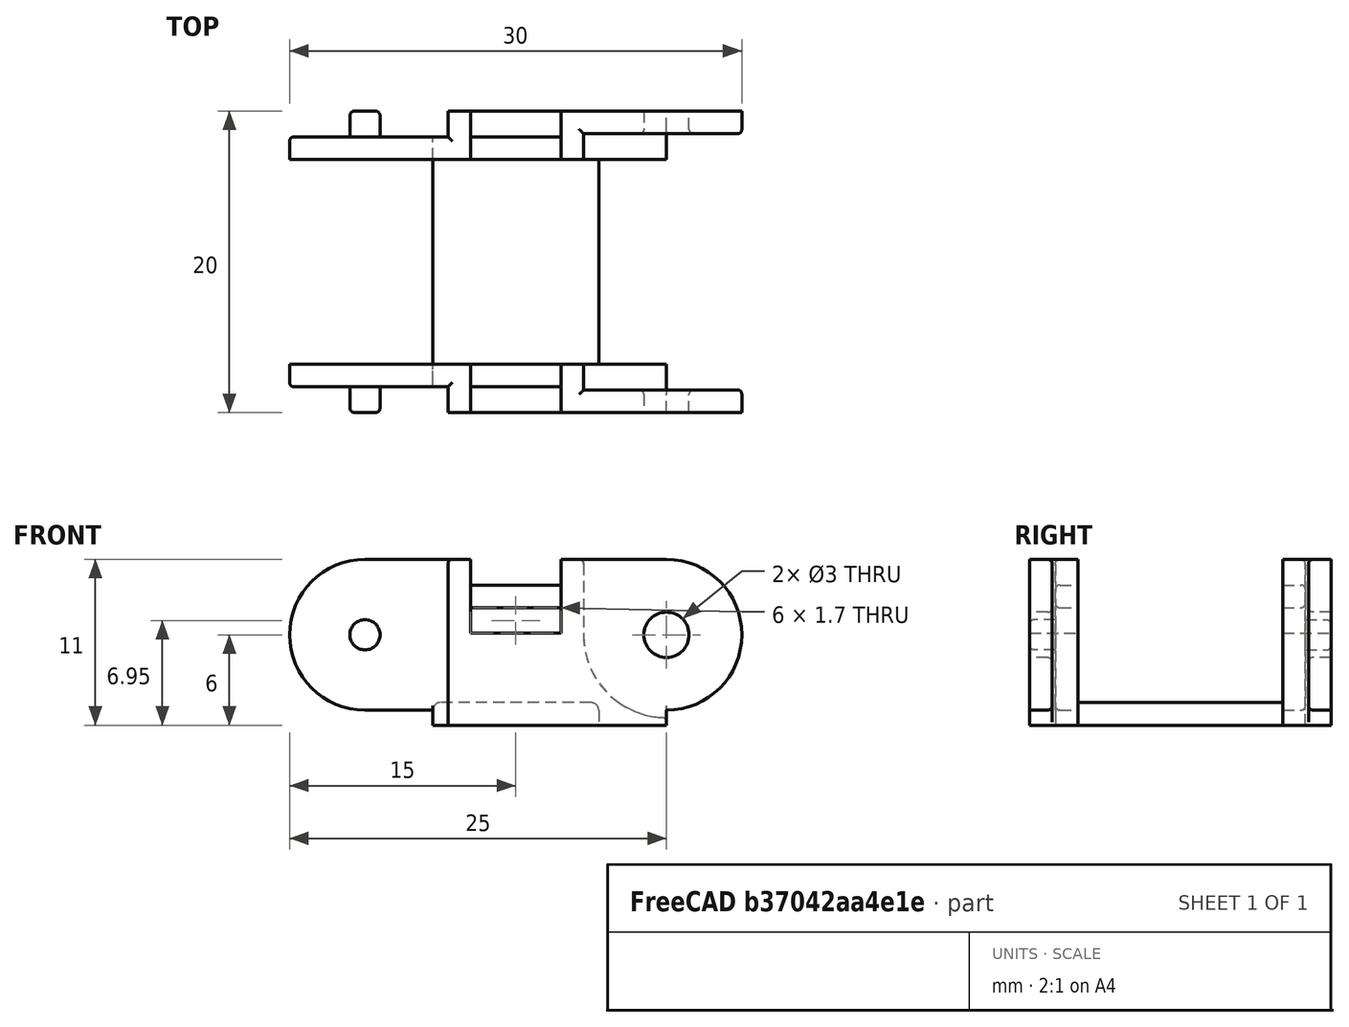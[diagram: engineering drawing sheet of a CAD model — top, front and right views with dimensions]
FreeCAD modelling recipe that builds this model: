
FCSTD DOCUMENT  (FreeCAD 0.17R13541 (Git))
Label: CableCareerNozzleHeader2
License: All rights reserved
LicenseURL: http://en.wikipedia.org/wiki/All_rights_reserved
objects: PartDesign::Fillet×20, Sketcher::SketchObject×8, PartDesign::Pocket×7, PartDesign::Pad×1, PartDesign::Body×1
note: 45 computed .brp shape members not serialized (recipe doc carries the construction recipe); baked Part::Feature solids carry a one-line shape summary decoded from their .brp

FEATURE [Sketcher::SketchObject] Sketch
  MapMode = 5
  Support = -> [XY_Plane]
  sketch-geometry (4):
    g0: LineSegment StartX=-15 StartY=10 StartZ=0 EndX=15 EndY=10 EndZ=0
    g1: LineSegment StartX=15 StartY=10 StartZ=0 EndX=15 EndY=-10 EndZ=0
    g2: LineSegment StartX=15 StartY=-10 StartZ=0 EndX=-15 EndY=-10 EndZ=0
    g3: LineSegment StartX=-15 StartY=-10 StartZ=0 EndX=-15 EndY=10 EndZ=0
  constraints (12):
    c: Coincident(g0,g1)
    c: Coincident(g1,g2)
    c: Coincident(g2,g3)
    c: Coincident(g3,g0)
    c: Horizontal(g0)
    c: Horizontal(g2)
    c: Vertical(g1)
    c: Vertical(g3)
    c: DistanceX(g0,g0) = 30
    c: DistanceY(g3,g3) = 20
    c: Distance(g-1,g3) = 15
    c: Distance(g-1,g0) = 10
FEATURE [PartDesign::Pad] Pad
  Length = 11
  Length2 = 100
  Profile = -> Sketch
  Type = 0
FEATURE [Sketcher::SketchObject] Sketch001
  ExternalGeometry = -> [Pad]
  MapMode = 5
  Placement = pos=(0,-10,0) rot=(1,0,0;1.5708rad)
  Support = -> [Pad]
  sketch-geometry (20):
    g0: ArcOfCircle CenterX=-10 CenterY=6 CenterZ=0 NormalX=0 NormalY=0 NormalZ=1 AngleXU=0 Radius=5 StartAngle=1.5708 EndAngle=4.71239
    g1: ArcOfCircle CenterX=10 CenterY=6 CenterZ=0 NormalX=0 NormalY=0 NormalZ=1 AngleXU=0 Radius=5 StartAngle=4.71239 EndAngle=7.85398
    g2: LineSegment StartX=-10 StartY=11 StartZ=0 EndX=-16 EndY=11 EndZ=0
    g3: LineSegment StartX=-16 StartY=11 StartZ=0 EndX=-16 EndY=0 EndZ=0
    g4: LineSegment StartX=-16 StartY=0 StartZ=0 EndX=-5.5 EndY=0 EndZ=0
    g5: LineSegment StartX=10 StartY=11 StartZ=0 EndX=16 EndY=11 EndZ=0
    g6: LineSegment StartX=16 StartY=11 StartZ=0 EndX=16 EndY=0 EndZ=0
    g7: LineSegment StartX=16 StartY=0 StartZ=0 EndX=10 EndY=0 EndZ=0
    g8: LineSegment StartX=10 StartY=0 StartZ=0 EndX=10 EndY=1 EndZ=0
    g9: LineSegment StartX=-3 StartY=11 StartZ=0 EndX=3 EndY=11 EndZ=0
    g10: LineSegment StartX=3 StartY=11 StartZ=0 EndX=3 EndY=9.3 EndZ=0
    g11: LineSegment StartX=3 StartY=9.3 StartZ=0 EndX=-3 EndY=9.3 EndZ=0
    g12: LineSegment StartX=-3 StartY=9.3 StartZ=0 EndX=-3 EndY=11 EndZ=0
    g13: LineSegment StartX=-3 StartY=7.8 StartZ=0 EndX=3 EndY=7.8 EndZ=0
    g14: LineSegment StartX=3 StartY=7.8 StartZ=0 EndX=3 EndY=6.1 EndZ=0
    g15: LineSegment StartX=3 StartY=6.1 StartZ=0 EndX=-3 EndY=6.1 EndZ=0
    g16: LineSegment StartX=-3 StartY=6.1 StartZ=0 EndX=-3 EndY=7.8 EndZ=0
    g17: Circle CenterX=10 CenterY=6 CenterZ=0 NormalX=0 NormalY=0 NormalZ=1 AngleXU=0 Radius=1.5
    g18: LineSegment StartX=-10 StartY=1 StartZ=0 EndX=-5.5 EndY=1 EndZ=0
    g19: LineSegment StartX=-5.5 StartY=1 StartZ=0 EndX=-5.5 EndY=0 EndZ=0
  constraints (61):
    c: DistanceX(g-3,g0) = 5
    c: DistanceY(g0,g-3) = 5
    c: Tangent(g0,g-5)
    c: PointOnObject(g0,g-3)
    c: Angle(g0) = 3.14159
    c: DistanceX(g1,g-6) = 5
    c: DistanceY(g1,g-6) = 5
    c: Tangent(g1,g-6)
    c: PointOnObject(g1,g-3)
    c: Angle(g1) = 3.14159
    c: Coincident(g2,g3)
    c: Coincident(g3,g4)
    c: Coincident(g5,g6)
    c: Coincident(g6,g7)
    c: Coincident(g7,g8)
    c: Horizontal(g7)
    c: Horizontal(g4)
    c: Horizontal(g2)
    c: Horizontal(g5)
    c: Vertical(g6)
    c: Vertical(g8)
    c: Vertical(g3)
    c: Coincident(g0,g2)
    c: Coincident(g5,g1)
    c: Coincident(g1,g8)
    c: PointOnObject(g-6,g7)
    c: PointOnObject(g-5,g4)
    c: DistanceX(g3,g-5) = 1
    c: DistanceX(g-6,g6) = 1
    c: Coincident(g9,g10)
    c: Coincident(g10,g11)
    c: Coincident(g11,g12)
    c: Coincident(g12,g9)
    c: Horizontal(g9)
    c: Horizontal(g11)
    c: Vertical(g10)
    c: Vertical(g12)
    c: Coincident(g13,g14)
    c: Coincident(g14,g15)
    c: Coincident(g15,g16)
    c: Coincident(g16,g13)
    c: Horizontal(g13)
    c: Horizontal(g15)
    c: Vertical(g14)
    c: Vertical(g16)
    c: PointOnObject(g9,g-3)
    c: DistanceX(g-5,g9) = 12
    c: DistanceX(g9,g-6) = 12
    c: DistanceY(g10,g10) = 1.7
    c: PointOnObject(g13,g12)
    c: PointOnObject(g13,g10)
    c: DistanceY(g13,g11) = 1.5
    c: DistanceY(g16,g16) = 1.7
    c: Coincident(g1,g17)
    c: Radius(g17) = 1.5
    c: Coincident(g18,g19)
    c: Horizontal(g18)
    c: Vertical(g19)
    c: Coincident(g18,g0)
    c: Coincident(g4,g19)
    c: DistanceX(g18,g18) = 4.5
FEATURE [PartDesign::Pocket] Pocket
  BaseFeature = -> Pad
  Length = 20
  Length2 = 100
  Profile = -> Sketch001
  Type = 0
FEATURE [Sketcher::SketchObject] Sketch002
  ExternalGeometry = -> [Pocket]
  MapMode = 5
  Placement = pos=(0,-10,0) rot=(1,0,0;1.5708rad)
  Support = -> [Pocket]
  sketch-geometry (9):
    g0: LineSegment StartX=-15 StartY=11 StartZ=0 EndX=-4.5 EndY=11 EndZ=0
    g1: LineSegment StartX=-4.5 StartY=11 StartZ=0 EndX=-4.5 EndY=0 EndZ=0
    g2: LineSegment StartX=-4.5 StartY=0 StartZ=0 EndX=-15 EndY=0 EndZ=0
    g3: LineSegment StartX=-15 StartY=0 StartZ=0 EndX=-15 EndY=11 EndZ=0
    g4: LineSegment StartX=-3 StartY=9.3 StartZ=0 EndX=3 EndY=9.3 EndZ=0
    g5: LineSegment StartX=3 StartY=9.3 StartZ=0 EndX=3 EndY=7.8 EndZ=0
    g6: LineSegment StartX=3 StartY=7.8 StartZ=0 EndX=-3 EndY=7.8 EndZ=0
    g7: LineSegment StartX=-3 StartY=7.8 StartZ=0 EndX=-3 EndY=9.3 EndZ=0
    g8: Circle CenterX=-10 CenterY=6 CenterZ=0 NormalX=0 NormalY=0 NormalZ=1 AngleXU=0 Radius=1
  constraints (24):
    c: Coincident(g0,g1)
    c: Coincident(g2,g3)
    c: Coincident(g3,g0)
    c: Horizontal(g0)
    c: Horizontal(g2)
    c: Vertical(g1)
    c: Vertical(g3)
    c: Coincident(g4,g5)
    c: Coincident(g5,g6)
    c: Coincident(g6,g7)
    c: Coincident(g7,g4)
    c: Horizontal(g4)
    c: Horizontal(g6)
    c: Vertical(g5)
    c: Vertical(g7)
    c: PointOnObject(g-3,g0)
    c: PointOnObject(g-3,g3)
    c: Coincident(g-3,g8)
    c: Radius(g8) = 1
    c: Coincident(g-5,g4)
    c: Coincident(g-6,g5)
    c: Coincident(g2,g1)
    c: PointOnObject(g-4,g2)
    c: DistanceX(g0,g4) = 1.5
FEATURE [Sketcher::SketchObject] Sketch003
  ExternalGeometry = -> [Pocket]
  MapMode = 5
  Placement = pos=(0,0,11) rot=(0,0,1;0rad)
  Support = -> [Pocket]
  sketch-geometry (4):
    g0: LineSegment StartX=-15 StartY=6.8 StartZ=0 EndX=15 EndY=6.8 EndZ=0
    g1: LineSegment StartX=15 StartY=6.8 StartZ=0 EndX=15 EndY=-6.8 EndZ=0
    g2: LineSegment StartX=15 StartY=-6.8 StartZ=0 EndX=-15 EndY=-6.8 EndZ=0
    g3: LineSegment StartX=-15 StartY=-6.8 StartZ=0 EndX=-15 EndY=6.8 EndZ=0
  constraints (12):
    c: Coincident(g0,g1)
    c: Coincident(g1,g2)
    c: Coincident(g2,g3)
    c: Coincident(g3,g0)
    c: Horizontal(g0)
    c: Horizontal(g2)
    c: Vertical(g1)
    c: Vertical(g3)
    c: PointOnObject(g2,g-3)
    c: PointOnObject(g1,g-4)
    c: DistanceY(g-4,g1) = 3.2
    c: DistanceY(g0,g-4) = 3.2
FEATURE [PartDesign::Pocket] Pocket001
  BaseFeature = -> Pocket
  Length = 9.5
  Length2 = 100
  Profile = -> Sketch003
  Type = 0
FEATURE [Sketcher::SketchObject] Sketch004
  ExternalGeometry = -> [Pocket001]
  MapMode = 5
  Placement = pos=(0,0,1.5) rot=(0,0,1;0rad)
  Support = -> [Pocket001]
  sketch-geometry (8):
    g0: LineSegment StartX=-12.1794 StartY=6.8 StartZ=0 EndX=-5.5 EndY=6.8 EndZ=0
    g1: LineSegment StartX=-5.5 StartY=6.8 StartZ=0 EndX=-5.5 EndY=-6.8 EndZ=0
    g2: LineSegment StartX=-5.5 StartY=-6.8 StartZ=0 EndX=-12.1794 EndY=-6.8 EndZ=0
    g3: LineSegment StartX=-12.1794 StartY=-6.8 StartZ=0 EndX=-12.1794 EndY=6.8 EndZ=0
    g4: LineSegment StartX=5.5 StartY=6.8 StartZ=0 EndX=12.1794 EndY=6.8 EndZ=0
    g5: LineSegment StartX=12.1794 StartY=6.8 StartZ=0 EndX=12.1794 EndY=-6.8 EndZ=0
    g6: LineSegment StartX=12.1794 StartY=-6.8 StartZ=0 EndX=5.5 EndY=-6.8 EndZ=0
    g7: LineSegment StartX=5.5 StartY=-6.8 StartZ=0 EndX=5.5 EndY=6.8 EndZ=0
  constraints (22):
    c: Coincident(g0,g1)
    c: Coincident(g1,g2)
    c: Coincident(g2,g3)
    c: Coincident(g3,g0)
    c: Horizontal(g0)
    c: Horizontal(g2)
    c: Vertical(g1)
    c: Vertical(g3)
    c: Coincident(g4,g5)
    c: Coincident(g5,g6)
    c: Coincident(g6,g7)
    c: Coincident(g7,g4)
    c: Horizontal(g4)
    c: Horizontal(g6)
    c: Vertical(g5)
    c: Vertical(g7)
    c: DistanceX(g4,g-5) = 4.5
    c: DistanceX(g-3,g0) = 4.5
    c: Coincident(g0,g-4)
    c: Coincident(g2,g-4)
    c: Coincident(g5,g-6)
    c: Coincident(g4,g-6)
FEATURE [PartDesign::Pocket] Pocket002
  BaseFeature = -> Pocket001
  Length = 1.5
  Length2 = 100
  Profile = -> Sketch004
  Type = 0
FEATURE [PartDesign::Pocket] Pocket003
  BaseFeature = -> Pocket002
  Length = 1.7
  Length2 = 100
  Profile = -> Sketch002
  Type = 0
FEATURE [Sketcher::SketchObject] Sketch005
  ExternalGeometry = -> [Pocket003]
  MapMode = 5
  Placement = pos=(0,10,0) rot=(0,0.707107,0.707107;3.14159rad)
  Support = -> [Pocket003]
  sketch-geometry (9):
    g0: LineSegment StartX=4.5 StartY=11 StartZ=0 EndX=15 EndY=11 EndZ=0
    g1: LineSegment StartX=15 StartY=11 StartZ=0 EndX=15 EndY=0 EndZ=0
    g2: LineSegment StartX=15 StartY=0 StartZ=0 EndX=4.5 EndY=0 EndZ=0
    g3: LineSegment StartX=4.5 StartY=0 StartZ=0 EndX=4.5 EndY=11 EndZ=0
    g4: LineSegment StartX=-3 StartY=9.3 StartZ=0 EndX=3 EndY=9.3 EndZ=0
    g5: LineSegment StartX=3 StartY=9.3 StartZ=0 EndX=3 EndY=7.8 EndZ=0
    g6: LineSegment StartX=3 StartY=7.8 StartZ=0 EndX=-3 EndY=7.8 EndZ=0
    g7: LineSegment StartX=-3 StartY=7.8 StartZ=0 EndX=-3 EndY=9.3 EndZ=0
    g8: Circle CenterX=10 CenterY=6 CenterZ=0 NormalX=0 NormalY=0 NormalZ=1 AngleXU=0 Radius=1
  constraints (24):
    c: Coincident(g0,g1)
    c: Coincident(g1,g2)
    c: Coincident(g3,g0)
    c: Horizontal(g0)
    c: Horizontal(g2)
    c: Vertical(g1)
    c: Vertical(g3)
    c: Coincident(g4,g5)
    c: Coincident(g5,g6)
    c: Coincident(g6,g7)
    c: Coincident(g7,g4)
    c: Horizontal(g4)
    c: Horizontal(g6)
    c: Vertical(g5)
    c: Vertical(g7)
    c: Coincident(g8,g-5)
    c: Coincident(g5,g-4)
    c: Coincident(g-3,g4)
    c: Coincident(g3,g2)
    c: DistanceX(g4,g0) = 1.5
    c: PointOnObject(g-5,g0)
    c: PointOnObject(g-5,g1)
    c: PointOnObject(g-6,g2)
    c: Radius(g8) = 1
FEATURE [PartDesign::Pocket] Pocket004
  BaseFeature = -> Pocket003
  Length = 1.7
  Length2 = 100
  Profile = -> Sketch005
  Type = 0
FEATURE [Sketcher::SketchObject] Sketch006
  ExternalGeometry = -> [Pocket004]
  MapMode = 5
  Placement = pos=(0,6.8,0) rot=(1,0,0;1.5708rad)
  Support = -> [Pocket004]
  sketch-geometry (3):
    g0: ArcOfCircle CenterX=10 CenterY=6 CenterZ=0 NormalX=0 NormalY=0 NormalZ=1 AngleXU=0 Radius=5.5 StartAngle=3.14159 EndAngle=7.85398
    g1: LineSegment StartX=4.5 StartY=6 StartZ=0 EndX=4.5 EndY=11.5 EndZ=0
    g2: LineSegment StartX=4.5 StartY=11.5 StartZ=0 EndX=10 EndY=11.5 EndZ=0
  constraints (7):
    c: Coincident(g1,g2)
    c: Horizontal(g2)
    c: Vertical(g1)
    c: Tangent(g0,g2) = 1.5708
    c: Tangent(g0,g1) = 1.5708
    c: Coincident(g0,g-3)
    c: Radius(g0) = 5.5
FEATURE [PartDesign::Pocket] Pocket005
  BaseFeature = -> Pocket004
  Length = 1.7
  Length2 = 100
  Profile = -> Sketch006
  Type = 0
FEATURE [Sketcher::SketchObject] Sketch007
  ExternalGeometry = -> [Pocket005]
  MapMode = 5
  Placement = pos=(0,-6.8,0) rot=(0,0.707107,0.707107;3.14159rad)
  Support = -> [Pocket005]
  sketch-geometry (3):
    g0: ArcOfCircle CenterX=-10 CenterY=6 CenterZ=0 NormalX=0 NormalY=0 NormalZ=1 AngleXU=0 Radius=5.5 StartAngle=1.5708 EndAngle=6.28319
    g1: LineSegment StartX=-10 StartY=11.5 StartZ=0 EndX=-4.5 EndY=11.5 EndZ=0
    g2: LineSegment StartX=-4.5 StartY=11.5 StartZ=0 EndX=-4.5 EndY=6 EndZ=0
  constraints (7):
    c: Coincident(g1,g2)
    c: Vertical(g2)
    c: Horizontal(g1)
    c: Tangent(g0,g1) = 1.5708
    c: Tangent(g2,g0) = 1.5708
    c: Coincident(g-3,g0)
    c: Radius(g0) = 5.5
FEATURE [PartDesign::Pocket] Pocket006
  BaseFeature = -> Pocket005
  Length = 1.7
  Length2 = 100
  Profile = -> Sketch007
  Type = 0
FEATURE [PartDesign::Fillet] Fillet
  Base = -> Pocket006 [Edge160]
  BaseFeature = -> Pocket006
  Radius = 0.3
FEATURE [PartDesign::Fillet] Fillet001
  Base = -> Fillet [Edge175]
  BaseFeature = -> Fillet
  Radius = 0.3
FEATURE [PartDesign::Fillet] Fillet002
  Base = -> Fillet001 [Edge132]
  BaseFeature = -> Fillet001
  Radius = 0.3
FEATURE [PartDesign::Fillet] Fillet003
  Base = -> Fillet002 [Edge151]
  BaseFeature = -> Fillet002
  Radius = 0.3
FEATURE [PartDesign::Fillet] Fillet004
  Base = -> Fillet003 [Edge21]
  BaseFeature = -> Fillet003
  Radius = 0.3
FEATURE [PartDesign::Fillet] Fillet005
  Base = -> Fillet004 [Edge5]
  BaseFeature = -> Fillet004
  Radius = 0.3
FEATURE [PartDesign::Fillet] Fillet006
  Base = -> Fillet005 [Edge15]
  BaseFeature = -> Fillet005
  Radius = 0.3
FEATURE [PartDesign::Fillet] Fillet007
  Base = -> Fillet006 [Edge138]
  BaseFeature = -> Fillet006
  Radius = 0.3
FEATURE [PartDesign::Fillet] Fillet008
  Base = -> Fillet007 [Edge47]
  BaseFeature = -> Fillet007
  Radius = 0.3
FEATURE [PartDesign::Fillet] Fillet009
  Base = -> Fillet008 [Edge80]
  BaseFeature = -> Fillet008
  Radius = 0.29
FEATURE [PartDesign::Fillet] Fillet010
  Base = -> Fillet009 [Edge52]
  BaseFeature = -> Fillet009
  Radius = 0.3
FEATURE [PartDesign::Fillet] Fillet011
  Base = -> Fillet010 [Edge53]
  BaseFeature = -> Fillet010
  Radius = 0.3
FEATURE [PartDesign::Fillet] Fillet012
  Base = -> Fillet011 [Edge225]
  BaseFeature = -> Fillet011
  Radius = 0.3
FEATURE [PartDesign::Fillet] Fillet013
  Base = -> Fillet012 [Edge52]
  BaseFeature = -> Fillet012
  Radius = 0.3
FEATURE [PartDesign::Fillet] Fillet014
  Base = -> Fillet013 [Edge106]
  BaseFeature = -> Fillet013
  Radius = 0.3
FEATURE [PartDesign::Fillet] Fillet015
  Base = -> Fillet014 [Edge6]
  BaseFeature = -> Fillet014
  Radius = 0.3
FEATURE [PartDesign::Fillet] Fillet016
  Base = -> Fillet015 [Edge120]
  BaseFeature = -> Fillet015
  Radius = 0.3
FEATURE [PartDesign::Fillet] Fillet017
  Base = -> Fillet016 [Edge48]
  BaseFeature = -> Fillet016
  Radius = 0.3
FEATURE [PartDesign::Fillet] Fillet018
  Base = -> Fillet017 [Edge96]
  BaseFeature = -> Fillet017
  Radius = 0.5
FEATURE [PartDesign::Fillet] Fillet019
  Base = -> Fillet018 [Edge58]
  BaseFeature = -> Fillet018
  Radius = 0.49
FEATURE [PartDesign::Body] Body
  Group = -> [Sketch,Pad,Sketch001,Pocket,Sketch002,Sketch003,Pocket001,Sketch004,Pocket002,Pocket003,Sketch005,Pocket004,Sketch006,Pocket005,Sketch007,Pocket006,Fillet,Fillet001,Fillet002,Fillet003,Fillet004,Fillet005,Fillet006,Fillet007,Fillet008,Fillet009,Fillet010,Fillet011,Fillet012,Fillet013,Fillet014,Fillet015,Fillet016,Fillet017,Fillet018,Fillet019]
  Origin = -> Origin
  Tip = -> Fillet019
